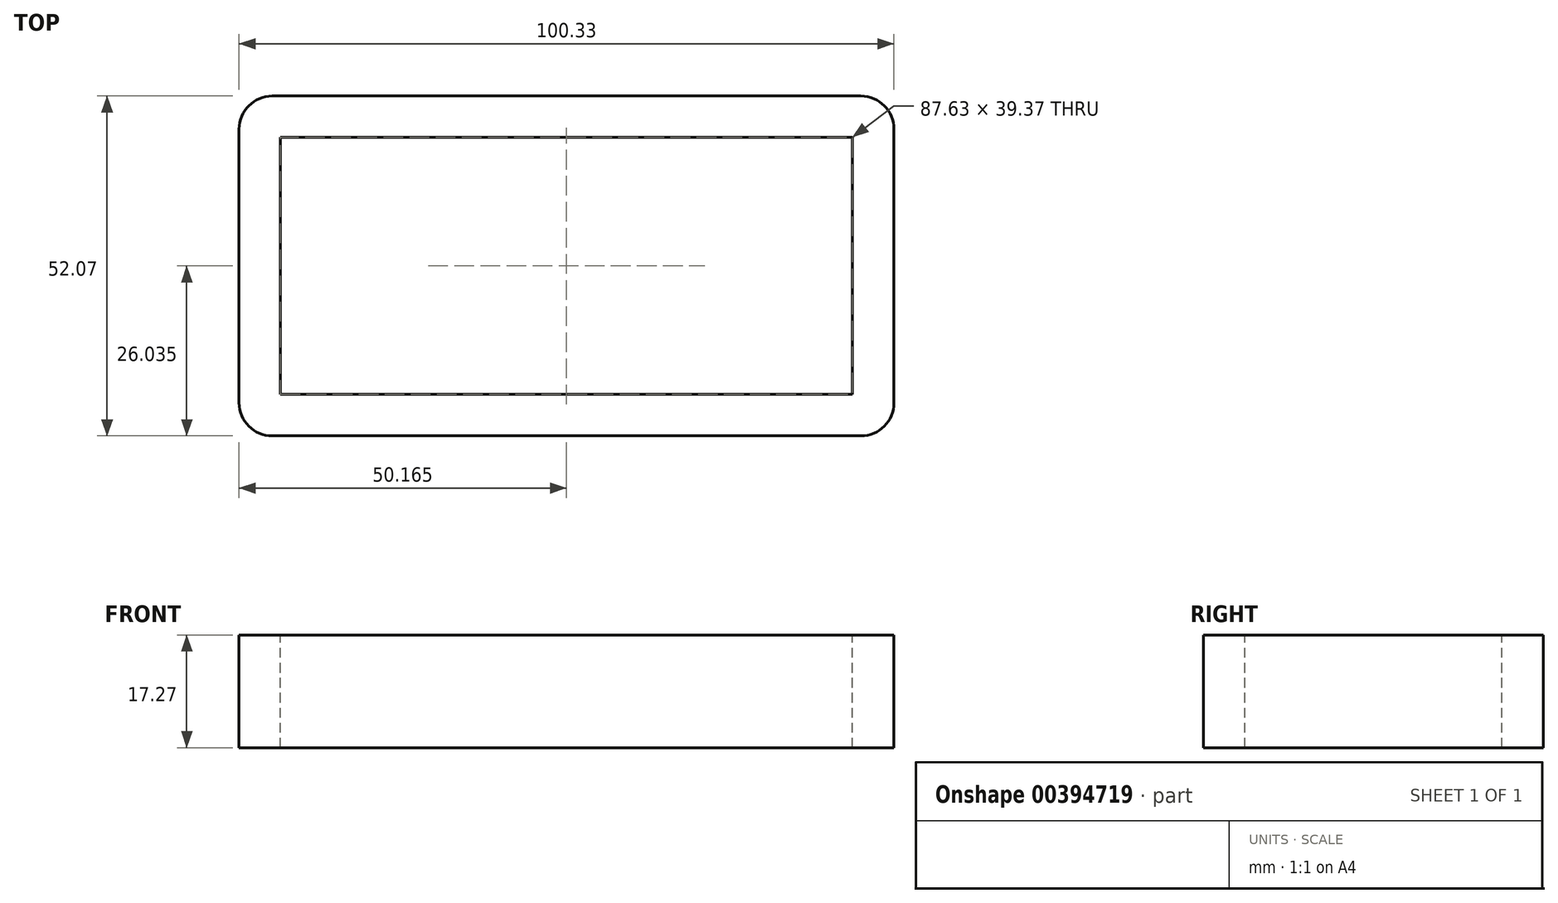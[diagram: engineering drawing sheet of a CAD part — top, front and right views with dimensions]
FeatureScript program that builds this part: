
annotation { "Feature Type Name" : "Feature", "Feature Type Description" : "" }
export const myFeature = defineFeature(function(context is Context, id is Id, definition is map)
    precondition{}
    {
        {
            var Q0;
            Q0=qCreatedBy(makeId("Top.planeOp"),FACE);
            var sketch = newSketch(context, id + "F0", { "sketchPlane" : qUnion([Q0])});
            skLineSegment(sketch, "E0.bottom", {"start": v(0, 0) * mm, "end": v(100.33, 0) * mm});
            skLineSegment(sketch, "E0.top", {"start": v(0, 52.07) * mm, "end": v(100.33, 52.07) * mm});
            skLineSegment(sketch, "E0.left", {"start": v(0, 0) * mm, "end": v(0, 52.07) * mm});
            skLineSegment(sketch, "E0.right", {"start": v(100.33, 0) * mm, "end": v(100.33, 52.07) * mm});
            skSolve(sketch);
        }
        {
            var Q0;
            Q0=makeQuery(id+"F0.imprint","IMPRINT",FACE,{"disambiguationData":[TD([[makeQuery(id+"F0.imprint","IMPRINT",EDGE,{"derivedFrom":sQuery(id+"F0.wireOp",EDGE,"E0.bottom")}),1.0]])]});
            extrude(context, id + "F1", {"entities" : qUnion([Q0]), "depth" : 17.27 * mm});
        }
        {
            var Q0;
            Q0=makeQuery(id+"F1.opExtrude","SWEPT_EDGE",EDGE,{"disambiguationData":[OSD([sQuery(id+"F0.wireOp",EDGE,"E0.top"),sQuery(id+"F0.wireOp",EDGE,"E0.left")])]});
            var Q1;
            Q1=makeQuery(id+"F1.opExtrude","SWEPT_EDGE",EDGE,{"disambiguationData":[OSD([sQuery(id+"F0.wireOp",EDGE,"E0.bottom"),sQuery(id+"F0.wireOp",EDGE,"E0.left")])]});
            var Q2;
            Q2=makeQuery(id+"F1.opExtrude","SWEPT_EDGE",EDGE,{"disambiguationData":[OSD([sQuery(id+"F0.wireOp",EDGE,"E0.bottom"),sQuery(id+"F0.wireOp",EDGE,"E0.right")])]});
            var Q3;
            Q3=makeQuery(id+"F1.opExtrude","SWEPT_EDGE",EDGE,{"disambiguationData":[OSD([sQuery(id+"F0.wireOp",EDGE,"E0.top"),sQuery(id+"F0.wireOp",EDGE,"E0.right")])]});
            fillet(context, id + "F2", {"entities" : qUnion([Q0, Q1, Q2, Q3]), "radius" : 5.08 * mm, "tangentPropagation" : true, "allowEdgeOverflow" : false});
        }
        {
            var Q0;
            Q0=makeQuery(id+"F1.opExtrude","CAP_FACE",FACE,{"disambiguationData":[OSD([sQuery(id+"F0.wireOp",EDGE,"E0.bottom"),sQuery(id+"F0.wireOp",EDGE,"E0.top"),sQuery(id+"F0.wireOp",EDGE,"E0.left"),sQuery(id+"F0.wireOp",EDGE,"E0.right")])],"isStart":false});
            var sketch = newSketch(context, id + "F3", { "sketchPlane" : qUnion([Q0])});
            skLineSegment(sketch, "E1.0", {"start": v(6.35, 6.35) * mm, "end": v(6.35, 45.72) * mm});
            skLineSegment(sketch, "E1.1", {"start": v(6.35, 6.35) * mm, "end": v(93.98, 6.35) * mm});
            skLineSegment(sketch, "E1.2", {"start": v(93.98, 6.35) * mm, "end": v(93.98, 45.72) * mm});
            skLineSegment(sketch, "E1.3", {"start": v(6.35, 45.72) * mm, "end": v(93.98, 45.72) * mm});
            skSolve(sketch);
        }
        {
            var Q0;
            Q0=makeQuery(id+"F3.imprint","IMPRINT",FACE,{"disambiguationData":[TD([[makeQuery(id+"F3.imprint","IMPRINT",EDGE,{"derivedFrom":sQuery(id+"F3.wireOp",EDGE,"E1.0")}),-1.0]])]});
            extrude(context, id + "F4", {"entities" : qUnion([Q0]), "operationType" : NewBodyOperationType.REMOVE, "oppositeDirection" : true, "depth" : 25.4 * mm});
        }
    });
